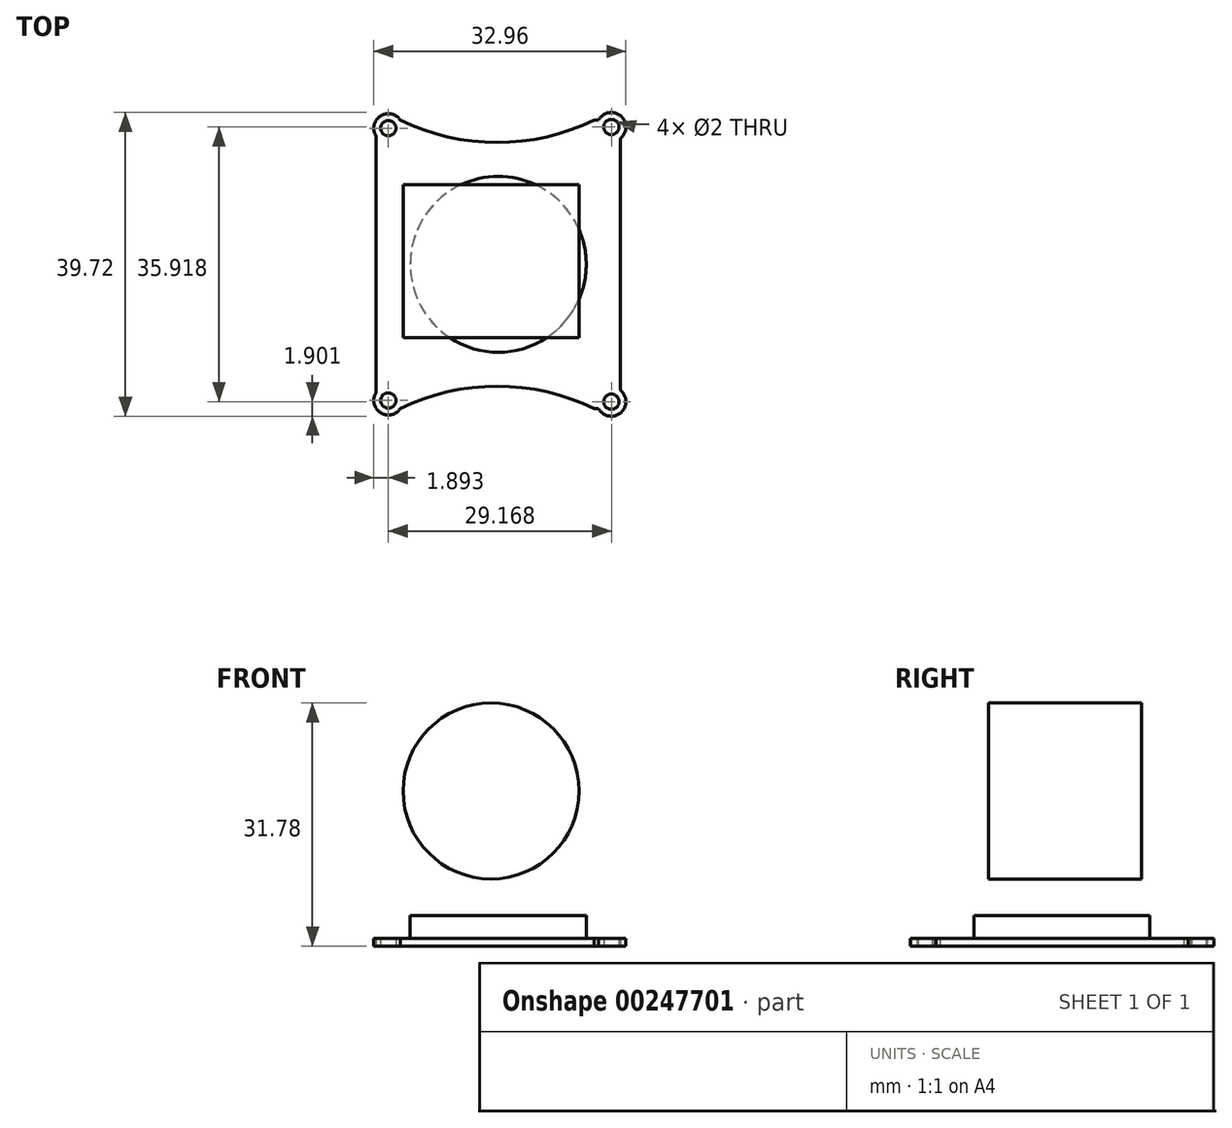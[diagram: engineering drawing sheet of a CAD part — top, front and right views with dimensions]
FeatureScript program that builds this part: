
annotation { "Feature Type Name" : "Feature", "Feature Type Description" : "" }
export const myFeature = defineFeature(function(context is Context, id is Id, definition is map)
    precondition{}
    {
        {
            var Q0;
            Q0=qCreatedBy(makeId("Top.planeOp"),FACE);
            var sketch = newSketch(context, id + "F0", { "sketchPlane" : qUnion([Q0])});
            skPoint(sketch, "E0.middle", {"position": v(0, 0) * mm});
            skPoint(sketch, "E1.startSnap0", {"position": v(0, -15.93) * mm});
            skArc(sketch, "E2", {"start": v(12.5, -18.84) * mm, "mid": v(-0.14, -15.93) * mm, "end": v(-12.79, -18.84) * mm});
            skArc(sketch, "E3", {"start": v(-15.97, -16.77) * mm, "mid": v(-15.41, -19.4) * mm, "end": v(-12.79, -18.84) * mm});
            skArc(sketch, "E4", {"start": v(13.11, -18.84) * mm, "mid": v(16, -19.42) * mm, "end": v(15.97, -16.47) * mm});
            skArc(sketch, "E5.MirrorCS", {"start": v(12.5, 18.84) * mm, "mid": v(-0.14, 15.93) * mm, "end": v(-12.79, 18.84) * mm});
            skArc(sketch, "E6.MirrorCS", {"start": v(-15.97, 16.77) * mm, "mid": v(-15.41, 19.4) * mm, "end": v(-12.79, 18.84) * mm});
            skArc(sketch, "E7.MirrorCS", {"start": v(13.11, 18.84) * mm, "mid": v(16, 19.42) * mm, "end": v(15.97, 16.47) * mm});
            skLineSegment(sketch, "E8", {"start": v(12.5, -18.84) * mm, "end": v(13.11, -18.84) * mm});
            skLineSegment(sketch, "E9", {"start": v(15.97, -16.47) * mm, "end": v(15.97, 16.47) * mm});
            skLineSegment(sketch, "E10", {"start": v(-15.97, -16.77) * mm, "end": v(-15.97, 16.77) * mm});
            skCircle(sketch, "E11", {"center": v(-14.38, -17.8) * mm, "radius": 1 * mm});
            skCircle(sketch, "E12", {"center": v(14.8, -17.96) * mm, "radius": 1 * mm});
            skCircle(sketch, "E13.MirrorC", {"center": v(-14.38, 17.8) * mm, "radius": 1 * mm});
            skCircle(sketch, "E14.MirrorC", {"center": v(14.8, 17.96) * mm, "radius": 1 * mm});
            skLineSegment(sketch, "E15", {"start": v(12.5, 18.84) * mm, "end": v(13.11, 18.84) * mm});
            skCircle(sketch, "E16", {"center": v(0, 0) * mm, "radius": 11.5 * mm});
            skSolve(sketch);
        }
        {
            var Q0;
            Q0=makeQuery(id+"F0.imprint","IMPRINT",FACE,{"disambiguationData":[TD([[makeQuery(id+"F0.imprint","IMPRINT",EDGE,{"derivedFrom":sQuery(id+"F0.wireOp",EDGE,"E2")}),-1.0]])]});
            extrude(context, id + "F1", {"entities" : qUnion([Q0]), "depth" : 1 * mm});
        }
        {
            var Q0;
            Q0=makeQuery(id+"F0.imprint","IMPRINT",FACE,{"disambiguationData":[TD([[makeQuery(id+"F0.imprint","IMPRINT",EDGE,{"derivedFrom":sQuery(id+"F0.wireOp",EDGE,"E16")}),1.0]])]});
            extrude(context, id + "F2", {"entities" : qUnion([Q0]), "operationType" : NewBodyOperationType.ADD, "depth" : 4 * mm});
        }
        {
            var Q0;
            Q0=makeQuery(id+"F2.opExtrude","CAP_FACE",FACE,{"disambiguationData":[OSD([sQuery(id+"F0.wireOp",EDGE,"E16")])],"isStart":false});
            var sketch = newSketch(context, id + "F3", { "sketchPlane" : qUnion([Q0])});
            skArc(sketch, "E17", {"start": v(4.4, 10.62) * mm, "mid": v(-0.92, 11.41) * mm, "end": v(-6.05, 9.78) * mm});
            skArc(sketch, "E18.MirrorCS", {"start": v(4.4, -10.62) * mm, "mid": v(-0.92, -11.41) * mm, "end": v(-6.05, -9.78) * mm});
            skArc(sketch, "E19", {"start": v(4.4, 10.62) * mm, "mid": v(-0.88, 10.9) * mm, "end": v(-6.05, 9.78) * mm});
            skArc(sketch, "E20.MirrorCS", {"start": v(4.4, -10.62) * mm, "mid": v(-0.88, -10.9) * mm, "end": v(-6.05, -9.78) * mm});
            skSolve(sketch);
        }
        {
            var Q0;
            Q0=sQuery(id+"F3.wireOp",EDGE,"E17");
            var Q1;
            Q1=sQuery(id+"F3.wireOp",EDGE,"E18.MirrorCS");
            var Q2;
            Q2=sQuery(id+"F3.wireOp",EDGE,"E20.MirrorCS");
            var Q3;
            Q3=sQuery(id+"F3.wireOp",EDGE,"E19");
            extrude(context, id + "F4", {"bodyType" : ToolBodyType.SURFACE, "surfaceEntities" : qUnion([Q0, Q1, Q2, Q3]), "depth" : 21 * mm});
        }
        {
            var Q0;
            Q0=qCreatedBy(makeId("Front.planeOp"),FACE);
            cPlane(context, id + "F5", {"entities" : qUnion([Q0]), "cplaneType" : CPlaneType.OFFSET, "offset" : 11.6 * mm, "width" : 150 * mm, "height" : 150 * mm});
        }
        {
            var Q0;
            Q0=qCreatedBy(id+"F5.planeOp",FACE);
            var sketch = newSketch(context, id + "F6", { "sketchPlane" : qUnion([Q0])});
            skCircle(sketch, "E21", {"center": v(-0.94, 20.28) * mm, "radius": 11.5 * mm});
            skSolve(sketch);
        }
        {
            var Q0;
            Q0=makeQuery(id+"F6.imprint","IMPRINT",FACE,{"disambiguationData":[TD([[makeQuery(id+"F6.imprint","IMPRINT",EDGE,{"derivedFrom":sQuery(id+"F6.wireOp",EDGE,"E21")}),1.0]])]});
            extrude(context, id + "F7", {"entities" : qUnion([Q0]), "oppositeDirection" : true, "depth" : 22 * mm, "hasSecondDirection" : true, "secondDirectionOppositeDirection" : true, "secondDirectionDepth" : 2 * mm});
        }
    });
